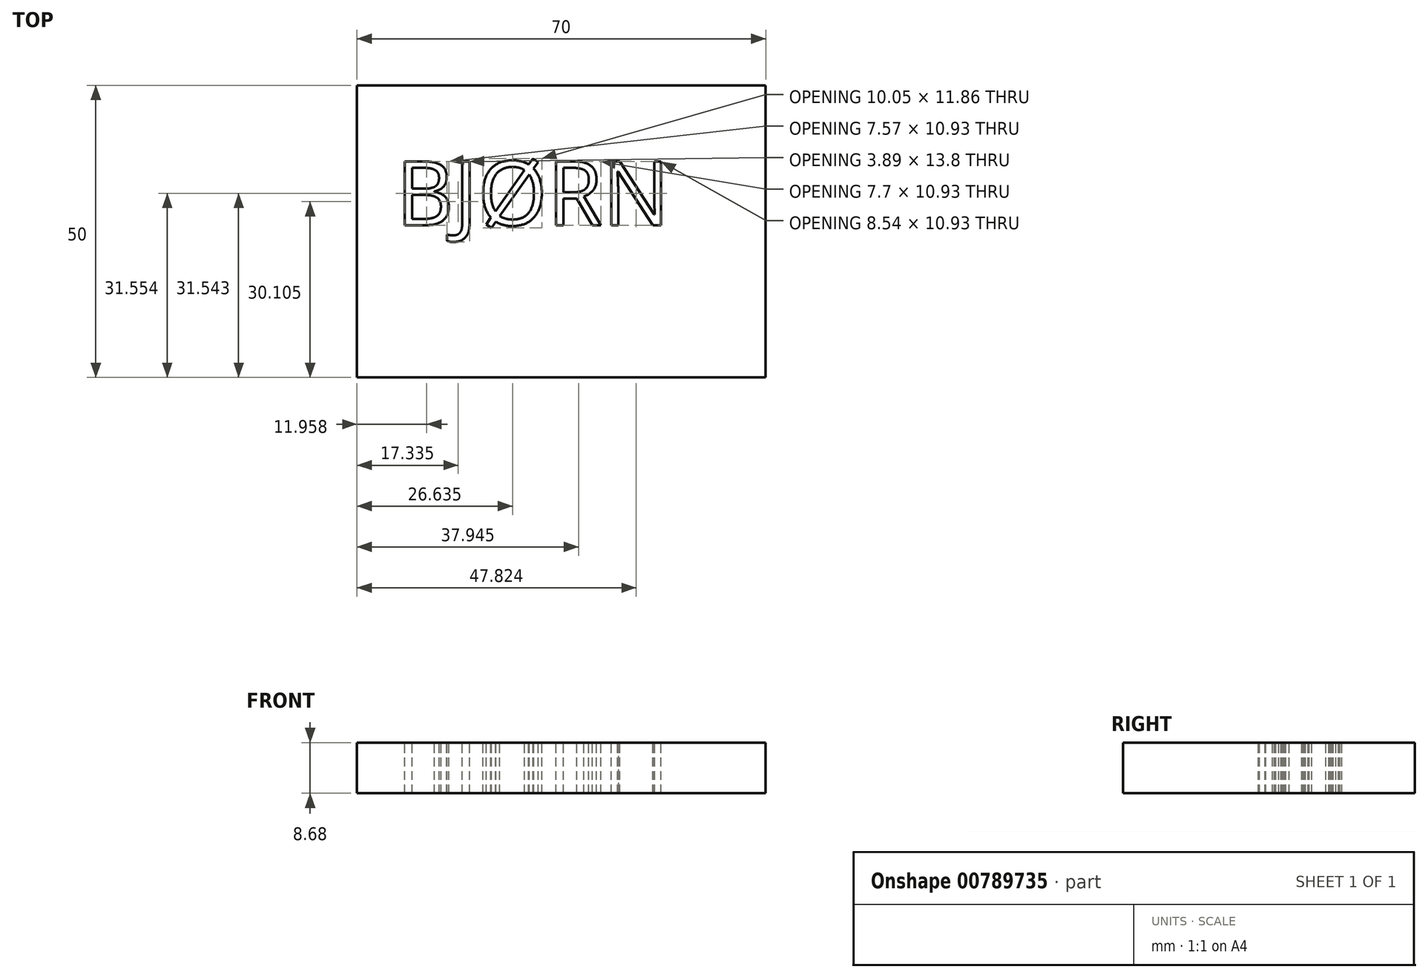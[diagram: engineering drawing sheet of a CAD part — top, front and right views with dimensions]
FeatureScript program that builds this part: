
annotation { "Feature Type Name" : "Feature", "Feature Type Description" : "" }
export const myFeature = defineFeature(function(context is Context, id is Id, definition is map)
    precondition{}
    {
        {
            var Q0;
            Q0=qCreatedBy(makeId("Top.planeOp"),FACE);
            var sketch = newSketch(context, id + "F0", { "sketchPlane" : qUnion([Q0])});
            skLineSegment(sketch, "E0.bottom", {"start": v(7.43, 63.38) * mm, "end": v(77.43, 63.38) * mm});
            skLineSegment(sketch, "E0.top", {"start": v(7.43, 13.38) * mm, "end": v(77.43, 13.38) * mm});
            skLineSegment(sketch, "E0.left", {"start": v(7.43, 63.38) * mm, "end": v(7.43, 13.38) * mm});
            skLineSegment(sketch, "E0.right", {"start": v(77.43, 63.38) * mm, "end": v(77.43, 13.38) * mm});
            skSolve(sketch);
        }
        {
            var Q0;
            Q0 = qSketchRegion(id + "F0", true);
            extrude(context, id + "F1", {"entities" : qUnion([Q0]), "depth" : 8.68 * mm, "offsetDistance" : 25 * mm});
        }
        {
            var Q0;
            Q0=makeQuery(id+"F1.opExtrude","CAP_FACE",FACE,{"disambiguationData":[OSD([sQuery(id+"F0.wireOp",EDGE,"E0.bottom"),sQuery(id+"F0.wireOp",EDGE,"E0.top"),sQuery(id+"F0.wireOp",EDGE,"E0.left"),sQuery(id+"F0.wireOp",EDGE,"E0.right")])],"isStart":false});
            var sketch = newSketch(context, id + "F2", { "sketchPlane" : qUnion([Q0])});
            skText(sketch, "E1", { "text": "BJØRN", "fontName": "OpenSans-Regular.ttf"});
            const initialGuessF2  = {"E1": [0.0141, 0.03946, 1, 0, 0.01102]};
            skSetInitialGuess(sketch, initialGuessF2);
            skSolve(sketch);
        }
        {
            var Q0;
            Q0=makeQuery(id+"F2.imprint","IMPRINT",FACE,{"disambiguationData":[TD([[makeQuery(id+"F2.imprint","IMPRINT",EDGE,{"derivedFrom":sQuery(id+"F2.wireOp",EDGE,"E1.sketch_text.stroke-0")}),-1.0]])]});
            var Q1;
            Q1=makeQuery(id+"F2.imprint","IMPRINT",FACE,{"disambiguationData":[TD([[makeQuery(id+"F2.imprint","IMPRINT",EDGE,{"derivedFrom":sQuery(id+"F2.wireOp",EDGE,"E1.sketch_text.stroke-25")}),-1.0]])]});
            var Q2;
            Q2=makeQuery(id+"F2.imprint","IMPRINT",FACE,{"disambiguationData":[TD([[makeQuery(id+"F2.imprint","IMPRINT",EDGE,{"derivedFrom":sQuery(id+"F2.wireOp",EDGE,"E1.sketch_text.stroke-35")}),-1.0]])]});
            var Q3;
            Q3=makeQuery(id+"F2.imprint","IMPRINT",FACE,{"disambiguationData":[TD([[makeQuery(id+"F2.imprint","IMPRINT",EDGE,{"derivedFrom":sQuery(id+"F2.wireOp",EDGE,"E1.sketch_text.stroke-59")}),-1.0]])]});
            var Q4;
            Q4=makeQuery(id+"F2.imprint","IMPRINT",FACE,{"disambiguationData":[TD([[makeQuery(id+"F2.imprint","IMPRINT",EDGE,{"derivedFrom":sQuery(id+"F2.wireOp",EDGE,"E1.sketch_text.stroke-77")}),-1.0]])]});
            extrude(context, id + "F3", {"entities" : qUnion([Q0, Q1, Q2, Q3, Q4]), "operationType" : NewBodyOperationType.REMOVE, "oppositeDirection" : true, "depth" : 25 * mm, "offsetDistance" : 25 * mm});
        }
    });
